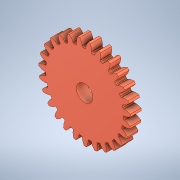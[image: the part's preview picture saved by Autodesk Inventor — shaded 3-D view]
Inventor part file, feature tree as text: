
AUTODESK INVENTOR PART (.ipt)
format: ipt  version: 2022 (Build 260153000, 153)  size: 436,736 bytes
history: imported  units: in
note: dims shown in document units (in); Inventor stores cm internally (conversion verified against a paired STEP export)
features: imported_body x1
ambient origin geometry x8: Origin, YZ Plane, XZ Plane, XY Plane, X Axis, Y Axis, Z Axis, Center Point
bodies: Solid1 (imported_parasolid), Body2 (imported_parasolid)
feature tree (1):
  imported_body  NMx_Import_Brep_tag  [imported B-rep: ~17 faces, bbox_mm=[18.405008, 11.321499, 4.1656]]
